# Revit family: HARMANN - REVIT- MOVO F400
name_source: partatom
category: Wyposażenie mechaniczne
units: mm (PartAtom-declared; Revit-internal decimal feet)

## family parameters
Numer OmniClass = 23.75.00.00
Oparty na płaszczyźnie roboczej = Nie
Punkt obliczania pomieszczeń = Nie
Tnij formami wycięć po wczytaniu = Nie
Typ części = Normalny
Tytuł OmniClass = Climate Control (HVAC)
Współdzielony = Nie
Wymiar okrągłego złącza = Użyj średnicy
Zachowaj orientację opisów = Nie
Zawsze pionowo = Tak

## types (22) — shared parameters
Autor = https://www.archispace.com
Klasa odporności ogniowej Tmax = 400 oC/2h
Lookup Table Name = MOVO
Opc Brak podstawy = Podstawa : Brak podstawy
Opc Podstawa Dachowa PR = Podstawa : Podstawa PR
Opis = Dachowy wentylator z wyrzutem poziomym F400
Podstawa A = Podstawa : Brak podstawy
Podstawa B = Podstawa : Podstawa PR
Producent = Harmann Polska Sp. z o.o.
Temperatura pracy ciągłej maksymalna T = 50 °C
Zasilanie Częstotliwość Maksymalna fmax = 50 Hz
Zasilanie Częstotliwość Minimalna fmin = 25 Hz
Zasilanie Częstotliwość Nominalna fnom = 50 Hz
Zasilanie Ilość faz = 3
Zasilanie napięcie nominalne Unom = 400 V
zero-valued in all types: Domyślna rzędna

## per-type parameters (varying)
| type | Akc D | Akc EP | Akc PR | Akc SL | Ciśnienie akustyczne nominalne obudowa Lpa | DN | MOVO | Masa | Model | N1 | Numer artykułu | Obroty nominalne nnom | Powietrze Przepływ Maksymalny Qmax | Powietrze ciśnienie statyczne maksymalne dPmax | Zasilanie Moc maksymalna Pmax | Zasilanie natężenie maksymalne Imax |
| MOVO 8-1000-32000T F400 | HARMANN - Akcesoria - D : D 900s | HARMANN - Akcesoria - EP : EP 900 | HARMANN - Akcesoria - PR : PR 1000/900 | HARMANN - Akcesoria - SL : SL 900 | 72 dB(A) | 900 mm  [stored 2.95276 ft] | HARMANN - Akcesoria - MOVO F400 : MOVO 8-1000-32000T F400 | 530.00 kg | MOVO 8-1000-32000T F400 | 12 mm | 02200221 | 725.000 obr./min | 32000.00 m³/h | 650.0 Pa | 7500 W | 16 A |
| MOVO 6-1000-52000T F400 | HARMANN - Akcesoria - D : D 900s | HARMANN - Akcesoria - EP : EP 900 | HARMANN - Akcesoria - PR : PR 1000/900 | HARMANN - Akcesoria - SL : SL 900 | 80 dB(A) | 900 mm  [stored 2.95276 ft] | HARMANN - Akcesoria - MOVO F400 : MOVO 6-1000-52000T F400 | 625.00 kg | MOVO 6-1000/52000T F400 | 12 mm | 02200211 | 980.000 obr./min | 52000.00 m³/h | 1330.0 Pa | 18500 W | 35 A |
| MOVO 8-900-27500T F400 | HARMANN - Akcesoria - D : D 800s | HARMANN - Akcesoria - EP : EP 800 | HARMANN - Akcesoria - PR : PR 900/800 | HARMANN - Akcesoria - SL : SL 800 | 71 dB(A) | 800 mm  [stored 2.62467 ft] | HARMANN - Akcesoria - MOVO F400 : MOVO 6-900-27500T F400 | 390.00 kg | MOVO 8-900/27500T F400 | 12 mm | 02200181 | 720.000 obr./min | 2750.00 m³/h | 590.0 Pa | 5500 W | 12 A |
| MOVO 6-800/26000T F400 | HARMANN - Akcesoria - D : D 710s | HARMANN - Akcesoria - EP : EP 710 | HARMANN - Akcesoria - PR : PR 710/630 | HARMANN - Akcesoria - SL : SL 710 | 73 dB(A) | 710 mm  [stored 2.3294 ft] | HARMANN - Akcesoria - MOVO F400 : MOVO 6-800/26000T F400 | 315.00 kg | MOVO 6-800/26000T F400 | 11 mm | 02200161 | 970.000 obr./min | 26000.00 m³/h | 750.0 Pa | 5500 W | 12 A |
| MOVO 4-800/39500T F400 | HARMANN - Akcesoria - D : D 710s | HARMANN - Akcesoria - EP : EP 710 | HARMANN - Akcesoria - PR : PR 710/630 | HARMANN - Akcesoria - SL : SL 710 | 82 dB(A) | 710 mm  [stored 2.3294 ft] | HARMANN - Akcesoria - MOVO F400 : MOVO 4-800/39500T F400 | 425.00 kg | MOVO 4-800/39500T | 11 mm | 02200162 | 1470.000 obr./min | 39500.00 m³/h | 1850.0 Pa | 18500 W | 35 A |
| MOVO 6-710/18300T F400 | HARMANN - Akcesoria - D : D 630s | HARMANN - Akcesoria - EP : EP 630 | HARMANN - Akcesoria - PR : PR 710/630 | HARMANN - Akcesoria - SL : SL 630 | 70 dB(A) | 630 mm  [stored 2.06693 ft] | HARMANN - Akcesoria - MOVO F400 : MOVO 6-710/18300T F400 | 285.00 kg | MOVO 6-710/18300T F400 | 9 mm | 02200131 | 1450.000 obr./min | 18300.00 m³/h | 700.0 Pa | 4000 W | 9 A |
| MOVO 4-710/27500T F400 | HARMANN - Akcesoria - D : D 630s | HARMANN - Akcesoria - EP : EP 630 | HARMANN - Akcesoria - PR : PR 710/630 | HARMANN - Akcesoria - SL : SL 630 | 79 dB(A) | 630 mm  [stored 2.06693 ft] | HARMANN - Akcesoria - MOVO F400 : MOVO 4-710/27500T F400 | 285.00 kg | MOVO 4-710/27500T F400 | 9 mm | 02200122 | 1450.000 obr./min | 27500.00 m³/h | 1500.0 Pa | 11000 W | 21 A |
| MOVO 6-710/15500T F400 | HARMANN - Akcesoria - D : D 630s | HARMANN - Akcesoria - EP : EP 630 | HARMANN - Akcesoria - PR : PR 710/630 | HARMANN - Akcesoria - SL : SL 630 | 68 | 630 mm  [stored 2.06693 ft] | HARMANN - Akcesoria - MOVO F400 : MOVO 6-710/15500T F400 | 255.00 kg | MOVO 6-710/15500T F400 | 9 mm | 02200121 | 970.000 obr./min | 15500.00 m³/h | 590.0 Pa | 3000 W | 7 A |
| MOVO 6-630/12400T F400 | HARMANN - Akcesoria - D : D 560s | HARMANN - Akcesoria - EP : EP 560 | HARMANN - Akcesoria - PR : PR 630/560 | HARMANN - Akcesoria - SL : SL 560 | 66 dB(A) | 560 mm  [stored 1.83727 ft] | HARMANN - Akcesoria - MOVO F400 : MOVO 6-630/12400T F400 | 163.00 kg | MOVO 6-630/12400T F400 | 7 mm | 0220101 | 940.000 obr./min | 12400.00 m³/h | 500.0 Pa | 2200 W | 5 A |
| MOVO 6-560/8700T F400 | HARMANN - Akcesoria - D : D 500s | HARMANN - Akcesoria - EP : EP 500 | HARMANN - Akcesoria - PR : PR 560/500 | HARMANN - Akcesoria - SL : SL 500 | 71 dB(A) | 500 mm  [stored 1.64042 ft] | HARMANN - Akcesoria - MOVO F400 : MOVO 6-560/8700T F400 | 116.00 kg | MOVO.S 6-560/8700T F400 | 6 mm | 02200081 | 930.000 obr./min | 8700.00 m³/h | 390.0 Pa | 1500 W | 4 A |
| MOVO 6-500/6100T F400 | HARMANN - Akcesoria - D : D 450s | HARMANN - Akcesoria - EP : EP 450 | HARMANN - Akcesoria - PR : PR 500/450 | HARMANN - Akcesoria - SL : SL 450 | 58 dB(A) | 450 mm  [stored 1.47638 ft] | HARMANN - Akcesoria - MOVO F400 : MOVO 6-500/6100T F400 | 83.00 kg | MOVO 6-500/6100T F400 | 3 mm | 02200061 | 895.000 obr./min | 6100.00 m³/h | 355.0 Pa | 550 W | 2 A |
| MOVO 6-450/4500T F400 | HARMANN - Akcesoria - D : D 400s | HARMANN - Akcesoria - EP : EP 400 | HARMANN - Akcesoria - PR : PR 450/400 | HARMANN - Akcesoria - SL : SL 400 | 56 dB(A) | 400 mm  [stored 1.31234 ft] | HARMANN - Akcesoria - MOVO F400 : MOVO 6-450/4500T F400 | 60.00 kg | MOVO  4-450/4500T F400 | 1 mm | 02200041 | 895.000 obr./min | 4500.00 m³/h | 250.0 Pa | 550 W | 2 A |
| MOVO 6-900-37000T F400 | HARMANN - Akcesoria - D : D 800s | HARMANN - Akcesoria - EP : EP 800 | HARMANN - Akcesoria - PR : PR 900/800 | HARMANN - Akcesoria - SL : SL 800 | 77 dB(A) | 800 mm  [stored 2.62467 ft] | HARMANN - Akcesoria - MOVO F400 : MOVO 6-900-37000T F400 | 415.00 kg | MOVO 6-900/37000T F400 | 12 mm | 02200171 | 970.000 obr./min | 37000.00 m³/h | 1150.0 Pa | 11000 W | 23 A |
| MOVO 6-1000/43100T F400 | HARMANN - Akcesoria - D : D 900s | HARMANN - Akcesoria - EP : EP 900 | HARMANN - Akcesoria - PR : PR 1000/900 | HARMANN - Akcesoria - SL : SL 900 | 78 dB(A) | 900 mm  [stored 2.95276 ft] | HARMANN - Akcesoria - MOVO F400 : MOVO 6-1000-52000T F400 | 580.00 kg | MOVO 6-1000/43100T | 12 mm | 02200201 | 975.000 obr./min | 43100.00 m³/h | 1200.0 Pa | 15000 W | 30 A |
| MOVO 4-800/36400T F400 | HARMANN - Akcesoria - D : D 710s | HARMANN - Akcesoria - EP : EP 710 | HARMANN - Akcesoria - PR : PR 710/630 | HARMANN - Akcesoria - SL : SL 710 | 81 dB(A) | 710 mm  [stored 2.3294 ft] | HARMANN - Akcesoria - MOVO F400 : MOVO 4-800/36400T F400 | 390.00 kg | MOVO 4-800/33400T F400 | 11 mm | 78252003 | 1460.000 obr./min | 36400.00 m³/h | 1800.0 Pa | 15000 W | 28 A |
| MOVO 4-710/23200T F400 | HARMANN - Akcesoria - D : D 630s | HARMANN - Akcesoria - EP : EP 630 | HARMANN - Akcesoria - PR : PR 710/630 | HARMANN - Akcesoria - SL : SL 630 | 78 dB(A) | 630 mm  [stored 2.06693 ft] | HARMANN - Akcesoria - MOVO F400 : MOVO 4-710/23200T F400 | 254.00 kg | MOVO 4-710/23200T F400 | 9 mm | 02200111 | 1450.000 obr./min | 23200.00 m³/h | 1305.0 Pa | 7500 W | 14 A |
| MOVO 4-630/19300T F400 | HARMANN - Akcesoria - D : D 560s | HARMANN - Akcesoria - EP : EP 560 | HARMANN - Akcesoria - PR : PR 630/560 | HARMANN - Akcesoria - SL : SL 560 | 75 dB(A) | 560 mm  [stored 1.83727 ft] | HARMANN - Akcesoria - MOVO F400 : MOVO 4-630/19300T F400 | 185.00 kg | MOVO 4-630/19300T F400 | 7 mm | 02200091 | 1455.000 obr./min | 19300.00 m³/h | 1200.0 Pa | 5500 W | 11 A |
| MOVO 4-560/13300T F400 | HARMANN - Akcesoria - D : D 500s | HARMANN - Akcesoria - EP : EP 500 | HARMANN - Akcesoria - PR : PR 560/500 | HARMANN - Akcesoria - SL : SL 500 | 71 dB(A) | 500 mm  [stored 1.64042 ft] | HARMANN - Akcesoria - MOVO F400 : MOVO 4-560/13300T F400 | 122.00 kg | MOVO 4-560/13300T F400 | 6 mm | 02200071 | 1425.000 obr./min | 13300.00 m³/h | 910.0 Pa | 3000 W | 6 A |
| MOVO 4-500/9100T F400 | HARMANN - Akcesoria - D : D 450s | HARMANN - Akcesoria - EP : EP 450 | HARMANN - Akcesoria - PR : PR 500/450 | HARMANN - Akcesoria - SL : SL 450 | 68 dB(A) | 450 mm  [stored 1.47638 ft] | HARMANN - Akcesoria - MOVO F400 : MOVO 4-500/9100T F400 | 92.00 kg | MOVO 4-500/9100T F400 | 3 mm | 02200051 | 1410.000 obr./min | 9100.00 m³/h | 655.0 Pa | 1500 W | 3 A |
| MOVO 4-450/6700T F400 | HARMANN - Akcesoria - D : D 400s | HARMANN - Akcesoria - EP : EP 400 | HARMANN - Akcesoria - PR : PR 450/400 | HARMANN - Akcesoria - SL : SL 400 | 65 dB(A) | 400 mm  [stored 1.31234 ft] | HARMANN - Akcesoria - MOVO F400 : MOVO 4-450/6700T F400 | 66.00 kg | MOVO 4-450/6700T F400 | 1 mm | 02200031 | 1385.000 obr./min | 6700.00 m³/h | 555.0 Pa | 1100 W | 3 A |
| MOVO 6-400/3100T F400 | HARMANN - Akcesoria - D : D 315s | HARMANN - Akcesoria - EP : EP 315 | HARMANN - Akcesoria - PR : PR 400/315 | HARMANN - Akcesoria - SL : SL 315 | 51 dB(A) | 315 mm  [stored 1.03346 ft] | HARMANN - Akcesoria - MOVO F400 : MOVO 6-400/3100T F400 | 48.00 kg | MOVO 6-400/3100T F400 | 1 mm | 02200021 | 910.000 obr./min | 3100.00 m³/h | 180.0 Pa | 370 W | 1 A |
| MOVO 4-400/4700T F400 | HARMANN - Akcesoria - D : D 315s | HARMANN - Akcesoria - EP : EP 315 | HARMANN - Akcesoria - PR : PR 400/315 | HARMANN - Akcesoria - SL : SL 315 | 80 dB(A) | 315 mm  [stored 1.03346 ft] | HARMANN - Akcesoria - MOVO F400 : MOVO 4-400/4700T F400 | 48.00 kg | MOVO 4-400/4700T F400 | 1 mm | 02200011 | 1405.000 obr./min | 4700.00 m³/h | 450.0 Pa | 550 W | 2 A |

note: [stored X ft] marks values corroborated as IEEE doubles in the binary element streams (Revit-internal decimal feet)

## geometry (parser evidence)
native form markers: Sweep x18
no freeform markers — native parametric forms only
